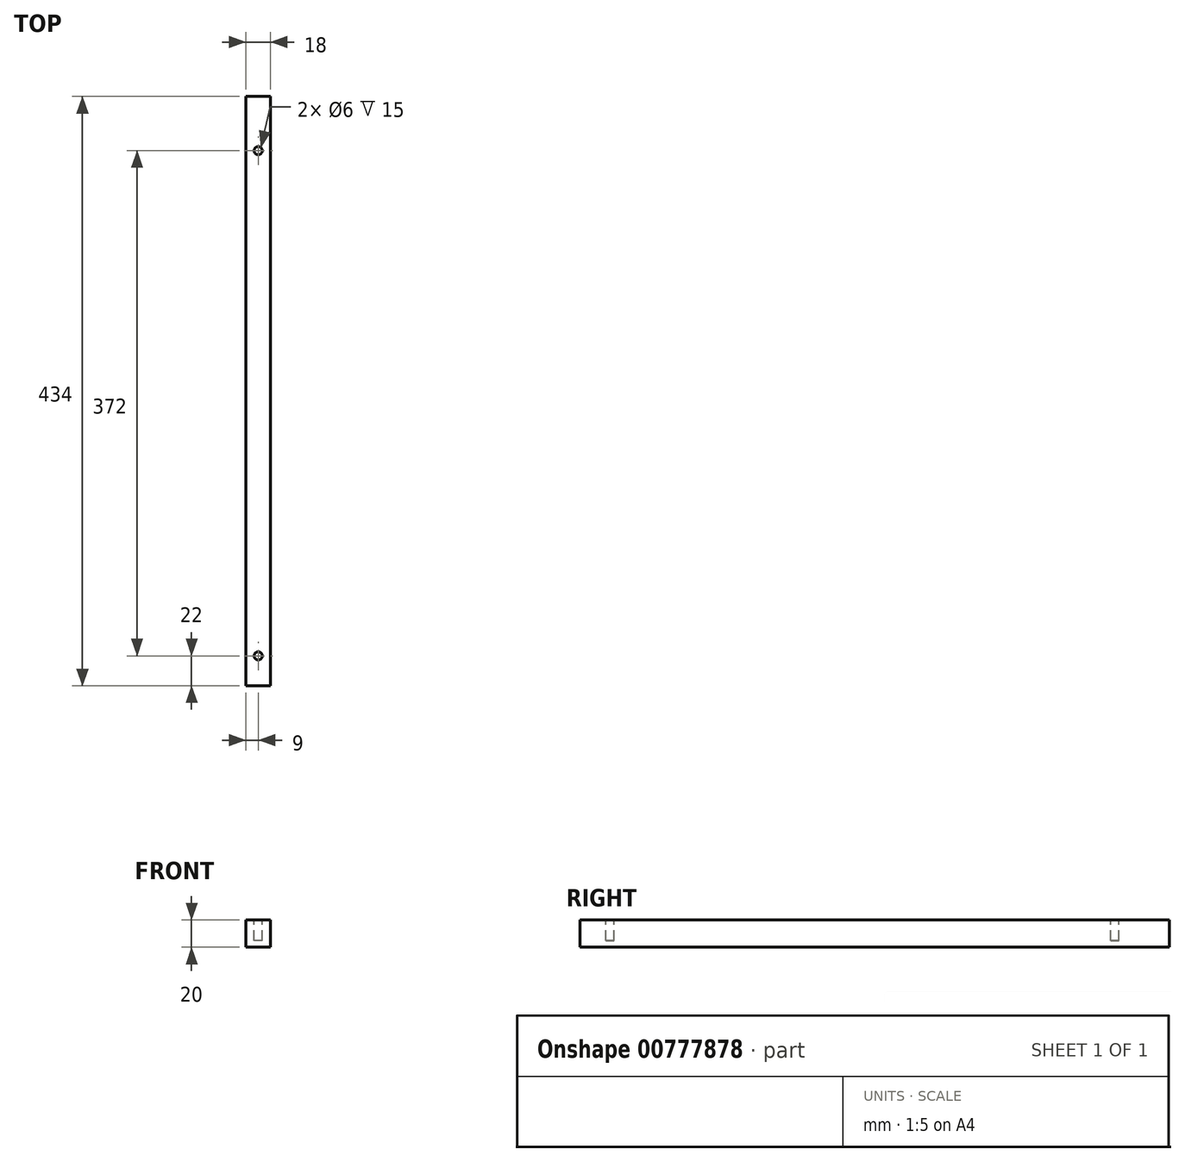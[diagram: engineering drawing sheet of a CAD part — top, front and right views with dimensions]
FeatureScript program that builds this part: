
annotation { "Feature Type Name" : "Feature", "Feature Type Description" : "" }
export const myFeature = defineFeature(function(context is Context, id is Id, definition is map)
    precondition{}
    {
        {
            var Q0;
            Q0=qCreatedBy(makeId("Top.planeOp"),FACE);
            var sketch = newSketch(context, id + "F0", { "sketchPlane" : qUnion([Q0])});
            skLineSegment(sketch, "E0.bottom", {"start": v(-9, 217) * mm, "end": v(9, 217) * mm});
            skLineSegment(sketch, "E0.top", {"start": v(-9, -217) * mm, "end": v(9, -217) * mm});
            skLineSegment(sketch, "E0.left", {"start": v(-9, 217) * mm, "end": v(-9, -217) * mm});
            skLineSegment(sketch, "E0.right", {"start": v(9, 217) * mm, "end": v(9, -217) * mm});
            skSolve(sketch);
        }
        {
            var Q0;
            Q0=qSketchRegion(id+"F0",true);
            extrude(context, id + "F1", {"entities" : qUnion([Q0]), "endBound" : BoundingType.SYMMETRIC, "depth" : 20 * mm, "offsetDistance" : 25 * mm});
        }
        {
            var Q0;
            Q0=makeQuery(id+"F1.opExtrude","CAP_FACE",FACE,{"disambiguationData":[OSD([sQuery(id+"F0.wireOp",EDGE,"E0.bottom"),sQuery(id+"F0.wireOp",EDGE,"E0.top"),sQuery(id+"F0.wireOp",EDGE,"E0.left"),sQuery(id+"F0.wireOp",EDGE,"E0.right")])],"isStart":false});
            var sketch = newSketch(context, id + "F2", { "sketchPlane" : qUnion([Q0])});
            skCircle(sketch, "E1", {"center": v(0, -195) * mm, "radius": 3 * mm});
            skCircle(sketch, "E2", {"center": v(0, 177) * mm, "radius": 3 * mm});
            skSolve(sketch);
        }
        {
            var Q0;
            Q0 = qSketchRegion(id + "F2", true);
            extrude(context, id + "F3", {"entities" : qUnion([Q0]), "operationType" : NewBodyOperationType.REMOVE, "oppositeDirection" : true, "depth" : 15 * mm, "offsetDistance" : 25 * mm});
        }
    });
